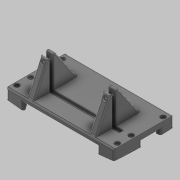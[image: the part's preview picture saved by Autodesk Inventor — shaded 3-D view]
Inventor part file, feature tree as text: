
AUTODESK INVENTOR PART (.ipt)
format: ipt  version: 2020 (Build 240168000, 168)  size: 7,925,248 bytes
history: native  units: in
note: dims shown in document units (in); Inventor stores cm internally (conversion verified against a paired STEP export)
features: sketch x17, extrude x13, plane x10, chamfer x8, other x6, revolve x3, split x3, hole x3, fillet x3, projected_geometry x2, sweep x1
ambient origin geometry x8: Origin, YZ Plane, XZ Plane, XY Plane, X Axis, Y Axis, Z Axis, Center Point
bodies: Solid7 (feature_tree), Solid8 (feature_tree), Solid10 (feature_tree)
feature tree (69):
  other  "ProfileTop"
  other  "ProfileSide"
  other  "XY_Project"
  other  "ProfileBack"
  revolve  "RevolvePlane"  [1 undecoded]
  revolve  "RevolveSketch"  [1 undecoded]
  extrude  "Extrusion5"  Depth=7.874in
  extrude  "Extrusion6"  Depth=5.4528in
  split  "Split1"
  revolve  "Revolution1"  [1 undecoded]
  chamfer  "Chamfer4"  Distance=1.6341in
  chamfer  "Chamfer5"  Distance=0.8398in
  chamfer  "Chamfer6"  [1 undecoded]
  chamfer  "Chamfer7"  Distance=0.5906in
  sweep  "Sweep1"
  chamfer  "Chamfer8"  Distance=0.1969in
  chamfer  "Chamfer9"  Distance=29.8893in
  chamfer  "Chamfer10"  Distance=8.1496in
  other  "SensorDivet"
  extrude  "Extrusion7"  Depth=0.3937in
  plane  "Work Plane6"
  plane  "Work Plane8"
  sketch  "Sketch12"  dims[d112=30.973in d142=7.874in]
  extrude  "BackSupport"  Depth=0.3937in
  extrude  "FrontSupport"  Depth=0.3937in
  plane  "Work Plane9"
  sketch  "Sketch19"  dims[d159=2.937in d160=16.7023in]
  sketch  "Sketch21"  dims[d161=16.7023in]
  extrude  "BaseVerticalExtend"  Depth=0.3937in
  plane  "Work Plane10"
  extrude  "BasePlate"  Depth=0.3937in
  extrude  "TriRib"  Depth=0.3937in
  extrude  "Slot"  Depth=0.3937in
  plane  "Work Plane11"
  extrude  "Extrusion19"  Depth=0.3937in TaperAngle=0.0deg
  extrude  "Extrusion20"  Depth=0.3937in TaperAngle=0.0deg
  hole  "Hole2"  [1 undecoded]
  fillet  "Fillet1"  Radius=1.4961in
  fillet  "Fillet2"  Radius=1.4961in
  fillet  "Fillet3"  Radius=5.4724in
  plane  "Work Plane13"
  split  "Split7"
  split  "Split8"
  plane  "Work Plane15"
  hole  "Hole3"  [1 undecoded]
  plane  "Work Plane16"
  hole  "Hole4"  [1 undecoded]
  chamfer  "Chamfer11"  Distance=0.1969in Angle=45.0deg
  plane  "Work Plane21"
  extrude  "Extrusion21"  Depth=0.3937in TaperAngle=45.0deg
  plane  "Work Plane22"
  extrude  "Extrusion22"  TaperAngle=0.0deg  [1 undecoded]
  other  "Image8"
  sketch  "Sketch9"  dims[d98=7.874in d109=2.278in]
  sketch  "3D Sketch1"
  sketch  "Sketch10"  dims[d110=12.4228in d111=3.715in]
  sketch  "Sketch13"  dims[d155=5.4528in d158=5.4528in]
  projected_geometry  "Projected Loop1"
  projected_geometry  "Projected Loop2"
  sketch  "Sketch22"  dims[d162=2.937in]
  sketch  "Sketch23"  dims[d170=1.8504in]
  sketch  "Sketch24"  dims[d171=7.4452in]
  sketch  "Sketch26"  dims[d172=5.4724in]
  sketch  "Sketch27"  dims[d173=0.0in]
  sketch  "Sketch29"  dims[d174=4.9332in]
  sketch  "Sketch32"  dims[d175=5.4231in]
  sketch  "Sketch33"  dims[d176=1.7487in]
  sketch  "Sketch34"  dims[d177=4.8557in]
  sketch  "Sketch35"  dims[d178=1.8083in d179=1.6341in d180=0.8398in d181=0.0in d187=0.5906in d188=0.1969in d189=0.1969in d272=29.8893in d278=8.1496in d279=1.2598in d280=10.9449in d281=6.8898in d282=1.2598in d283=5.4724in d284=5.4724in d285=8.1496in d288=15.748in d289=0.0in d290=15.748in d291=0.0in d346=180.0deg d347=1.4961in d348=1.4961in d349=5.4724in d350=0.1969in d351=1.4961in d352=45.0deg d353=0.1969in d354=1.4961in d355=45.0deg d356=0.1969in d357=1.4961in d358=45.0deg d359=0.1969in d360=1.4961in d361=45.0deg d362=0.0in d363=0.0in d364=0.1969in d365=1.4961in d366=45.0deg d367=0.1969in d368=1.4961in d369=45.0deg d370=0.0591in d371=1.4961in d372=45.0deg d373=-1.9685in d375=0.0in d376=0.0in d377=1.4961in d378=1.4961in d379=0.0in d380=0.6693in d381=0.6693in d382=0.6693in d383=0.6693in d384=0.6693in d385=0.6693in d386=0.5512in d387=0.9055in d388=0.0in d397=-1.9685in d424=0.3937in d425=0.0in d426=1.9685in d427=0.0in d428=12.2047in d429=3.1496in d430=6.1024in d431=0.5906in d432=12.2047in d433=6.1024in d434=1.5748in d457=0.3937in d458=0.0in d459=0.0in d460=0.5906in d461=0.0in d462=3.1496in d463=3.1496in d464=0.7874in d465=0.7874in d466=4.9213in d467=4.9213in d468=0.1969in d469=0.1969in d470=3.937in d471=0.0in d479=0.4094in d480=0.7953in d481=0.0in d482=4.2126in d483=4.2126in d484=8.6693in d485=0.0in d490=-2.3622in d491=0.7874in d492=0.7874in d493=1.1811in d494=0.0in d495=0.7874in d496=0.7874in d497=0.7874in d498=0.0in d512=0.3937in d513=0.3937in d514=0.3937in d515=0.3937in d516=0.7874in d517=0.7874in d518=0.7874in d519=0.7874in d520=0.3937in d521=0.3937in d522=0.7874in d523=0.7874in d524=0.3307in d525=0.2362in d526=0.5669in d527=0.2756in d528=90.0deg d529=2.3622in d530=0.8108in d532=0.1969in d533=0.1575in d534=0.1575in d535=1.1811in d541=1.3061in d542=3.2283in d543=3.2283in d544=0.3307in d545=0.2362in d546=0.5512in d547=0.2756in d548=90.0deg d549=2.3622in d550=0.8108in d551=0.3937in d552=0.3937in d553=0.9936in d554=3.2283in d555=3.2283in d556=0.3937in d557=0.3937in d558=0.3307in d559=0.2362in d560=0.5512in d561=0.2756in d562=90.0deg d563=2.3622in d564=0.8108in d565=1.9685in d572=0.0394in d573=0.0787in d574=45.0deg d575=4.625in d576=0.0in d577=0.0in d578=0.4375in d579=0.0in d580=0.0in d163=0.0197in d164=0.0344in d165=0.0197in d166=0.0344in d440=0.0197in d441=0.0344in d442=0.0197in d443=0.0344in d449=0.0197in d450=0.0344in d451=0.0197in d452=0.0344in d540=0.0394in]
note: 8 required parameter values undecoded (feature->parameter linkage not recoverable at this tier; creation-order binding heuristic only, values carry confidence <= 0.55)